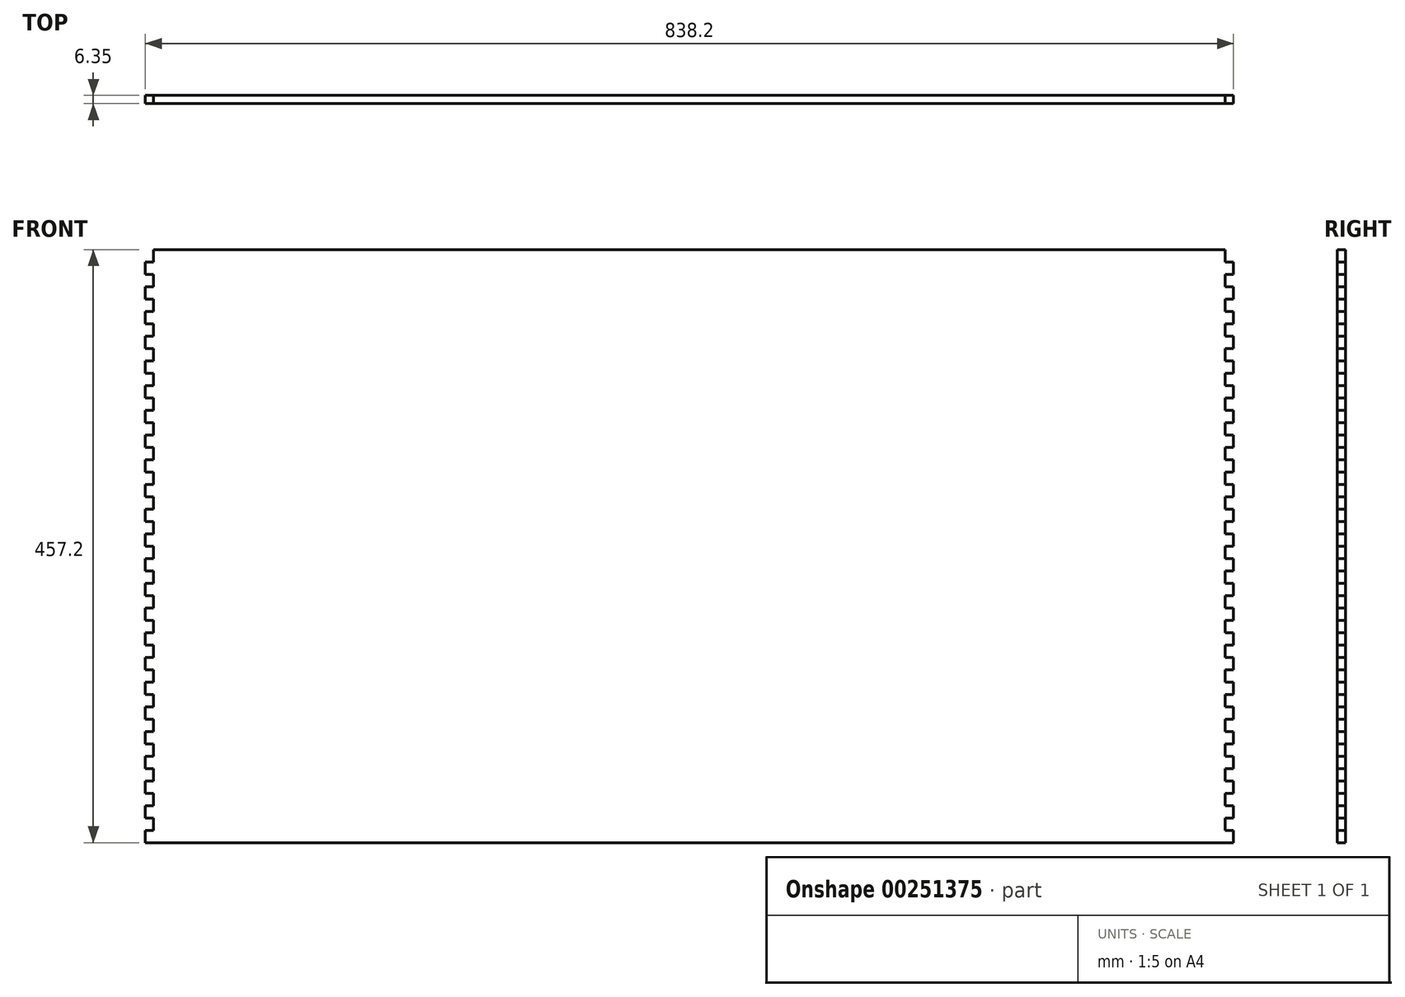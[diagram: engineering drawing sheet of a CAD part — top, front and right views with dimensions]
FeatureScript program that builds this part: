
annotation { "Feature Type Name" : "Feature", "Feature Type Description" : "" }
export const myFeature = defineFeature(function(context is Context, id is Id, definition is map)
    precondition{}
    {
        {
            var Q0;
            Q0=qCreatedBy(makeId("Front.planeOp"),FACE);
            var sketch = newSketch(context, id + "F0", { "sketchPlane" : qUnion([Q0])});
            skLineSegment(sketch, "E0.bottom", {"start": v(412.75, 228.6) * mm, "end": v(-412.75, 228.6) * mm});
            skLineSegment(sketch, "E0.top", {"start": v(419.1, -228.6) * mm, "end": v(-419.1, -228.6) * mm});
            skPoint(sketch, "E0.middle", {"position": v(0, 0) * mm});
            skLineSegment(sketch, "E1", {"start": v(412.75, 228.6) * mm, "end": v(412.75, 219.08) * mm});
            skLineSegment(sketch, "E2", {"start": v(412.75, 219.08) * mm, "end": v(419.1, 219.08) * mm});
            skLineSegment(sketch, "E3.0.1.0", {"start": v(412.75, 209.55) * mm, "end": v(412.75, 200.03) * mm});
            skLineSegment(sketch, "E3.0.1.1", {"start": v(412.75, 200.03) * mm, "end": v(419.1, 200.03) * mm});
            skLineSegment(sketch, "E3.0.1.3", {"start": v(419.1, 209.55) * mm, "end": v(412.75, 209.55) * mm});
            skLineSegment(sketch, "E3.0.2.0", {"start": v(412.75, 190.5) * mm, "end": v(412.75, 180.98) * mm});
            skLineSegment(sketch, "E3.0.2.1", {"start": v(412.75, 180.98) * mm, "end": v(419.1, 180.98) * mm});
            skLineSegment(sketch, "E3.0.2.3", {"start": v(419.1, 190.5) * mm, "end": v(412.75, 190.5) * mm});
            skLineSegment(sketch, "E3.0.3.0", {"start": v(412.75, 171.45) * mm, "end": v(412.75, 161.93) * mm});
            skLineSegment(sketch, "E3.0.3.1", {"start": v(412.75, 161.93) * mm, "end": v(419.1, 161.93) * mm});
            skLineSegment(sketch, "E3.0.3.3", {"start": v(419.1, 171.45) * mm, "end": v(412.75, 171.45) * mm});
            skLineSegment(sketch, "E3.0.4.0", {"start": v(412.75, 152.4) * mm, "end": v(412.75, 142.88) * mm});
            skLineSegment(sketch, "E3.0.4.1", {"start": v(412.75, 142.88) * mm, "end": v(419.1, 142.88) * mm});
            skLineSegment(sketch, "E3.0.4.3", {"start": v(419.1, 152.4) * mm, "end": v(412.75, 152.4) * mm});
            skLineSegment(sketch, "E3.0.5.0", {"start": v(412.75, 133.35) * mm, "end": v(412.75, 123.83) * mm});
            skLineSegment(sketch, "E3.0.5.1", {"start": v(412.75, 123.83) * mm, "end": v(419.1, 123.83) * mm});
            skLineSegment(sketch, "E3.0.5.3", {"start": v(419.1, 133.35) * mm, "end": v(412.75, 133.35) * mm});
            skLineSegment(sketch, "E3.0.6.0", {"start": v(412.75, 114.3) * mm, "end": v(412.75, 104.78) * mm});
            skLineSegment(sketch, "E3.0.6.1", {"start": v(412.75, 104.78) * mm, "end": v(419.1, 104.78) * mm});
            skLineSegment(sketch, "E3.0.6.3", {"start": v(419.1, 114.3) * mm, "end": v(412.75, 114.3) * mm});
            skLineSegment(sketch, "E3.0.7.0", {"start": v(412.75, 95.25) * mm, "end": v(412.75, 85.73) * mm});
            skLineSegment(sketch, "E3.0.7.1", {"start": v(412.75, 85.73) * mm, "end": v(419.1, 85.73) * mm});
            skLineSegment(sketch, "E3.0.7.3", {"start": v(419.1, 95.25) * mm, "end": v(412.75, 95.25) * mm});
            skLineSegment(sketch, "E3.0.8.0", {"start": v(412.75, 76.2) * mm, "end": v(412.75, 66.68) * mm});
            skLineSegment(sketch, "E3.0.8.1", {"start": v(412.75, 66.68) * mm, "end": v(419.1, 66.68) * mm});
            skLineSegment(sketch, "E3.0.8.3", {"start": v(419.1, 76.2) * mm, "end": v(412.75, 76.2) * mm});
            skLineSegment(sketch, "E3.0.9.0", {"start": v(412.75, 57.15) * mm, "end": v(412.75, 47.63) * mm});
            skLineSegment(sketch, "E3.0.9.1", {"start": v(412.75, 47.63) * mm, "end": v(419.1, 47.63) * mm});
            skLineSegment(sketch, "E3.0.9.3", {"start": v(419.1, 57.15) * mm, "end": v(412.75, 57.15) * mm});
            skLineSegment(sketch, "E3.0.10.0", {"start": v(412.75, 38.1) * mm, "end": v(412.75, 28.58) * mm});
            skLineSegment(sketch, "E3.0.10.1", {"start": v(412.75, 28.58) * mm, "end": v(419.1, 28.58) * mm});
            skLineSegment(sketch, "E3.0.10.3", {"start": v(419.1, 38.1) * mm, "end": v(412.75, 38.1) * mm});
            skLineSegment(sketch, "E3.0.11.0", {"start": v(412.75, 19.05) * mm, "end": v(412.75, 9.53) * mm});
            skLineSegment(sketch, "E3.0.11.1", {"start": v(412.75, 9.53) * mm, "end": v(419.1, 9.53) * mm});
            skLineSegment(sketch, "E3.0.11.3", {"start": v(419.1, 19.05) * mm, "end": v(412.75, 19.05) * mm});
            skLineSegment(sketch, "E3.0.12.0", {"start": v(412.75, 0) * mm, "end": v(412.75, -9.52) * mm});
            skLineSegment(sketch, "E3.0.12.1", {"start": v(412.75, -9.52) * mm, "end": v(419.1, -9.52) * mm});
            skLineSegment(sketch, "E3.0.12.3", {"start": v(419.1, 0) * mm, "end": v(412.75, 0) * mm});
            skLineSegment(sketch, "E3.0.13.0", {"start": v(412.75, -19.05) * mm, "end": v(412.75, -28.57) * mm});
            skLineSegment(sketch, "E3.0.13.1", {"start": v(412.75, -28.57) * mm, "end": v(419.1, -28.57) * mm});
            skLineSegment(sketch, "E3.0.13.3", {"start": v(419.1, -19.05) * mm, "end": v(412.75, -19.05) * mm});
            skLineSegment(sketch, "E3.0.14.0", {"start": v(412.75, -38.1) * mm, "end": v(412.75, -47.62) * mm});
            skLineSegment(sketch, "E3.0.14.1", {"start": v(412.75, -47.62) * mm, "end": v(419.1, -47.62) * mm});
            skLineSegment(sketch, "E3.0.14.3", {"start": v(419.1, -38.1) * mm, "end": v(412.75, -38.1) * mm});
            skLineSegment(sketch, "E3.0.15.0", {"start": v(412.75, -57.15) * mm, "end": v(412.75, -66.67) * mm});
            skLineSegment(sketch, "E3.0.15.1", {"start": v(412.75, -66.67) * mm, "end": v(419.1, -66.67) * mm});
            skLineSegment(sketch, "E3.0.15.3", {"start": v(419.1, -57.15) * mm, "end": v(412.75, -57.15) * mm});
            skLineSegment(sketch, "E3.0.16.0", {"start": v(412.75, -76.2) * mm, "end": v(412.75, -85.72) * mm});
            skLineSegment(sketch, "E3.0.16.1", {"start": v(412.75, -85.72) * mm, "end": v(419.1, -85.72) * mm});
            skLineSegment(sketch, "E3.0.16.3", {"start": v(419.1, -76.2) * mm, "end": v(412.75, -76.2) * mm});
            skLineSegment(sketch, "E3.0.17.0", {"start": v(412.75, -95.25) * mm, "end": v(412.75, -104.77) * mm});
            skLineSegment(sketch, "E3.0.17.1", {"start": v(412.75, -104.77) * mm, "end": v(419.1, -104.77) * mm});
            skLineSegment(sketch, "E3.0.17.3", {"start": v(419.1, -95.25) * mm, "end": v(412.75, -95.25) * mm});
            skLineSegment(sketch, "E3.0.18.0", {"start": v(412.75, -114.3) * mm, "end": v(412.75, -123.82) * mm});
            skLineSegment(sketch, "E3.0.18.1", {"start": v(412.75, -123.82) * mm, "end": v(419.1, -123.82) * mm});
            skLineSegment(sketch, "E3.0.18.3", {"start": v(419.1, -114.3) * mm, "end": v(412.75, -114.3) * mm});
            skLineSegment(sketch, "E3.0.19.0", {"start": v(412.75, -133.35) * mm, "end": v(412.75, -142.87) * mm});
            skLineSegment(sketch, "E3.0.19.1", {"start": v(412.75, -142.87) * mm, "end": v(419.1, -142.87) * mm});
            skLineSegment(sketch, "E3.0.19.3", {"start": v(419.1, -133.35) * mm, "end": v(412.75, -133.35) * mm});
            skLineSegment(sketch, "E3.0.20.0", {"start": v(412.75, -152.4) * mm, "end": v(412.75, -161.92) * mm});
            skLineSegment(sketch, "E3.0.20.1", {"start": v(412.75, -161.92) * mm, "end": v(419.1, -161.92) * mm});
            skLineSegment(sketch, "E3.0.20.3", {"start": v(419.1, -152.4) * mm, "end": v(412.75, -152.4) * mm});
            skLineSegment(sketch, "E3.0.21.0", {"start": v(412.75, -171.45) * mm, "end": v(412.75, -180.97) * mm});
            skLineSegment(sketch, "E3.0.21.1", {"start": v(412.75, -180.97) * mm, "end": v(419.1, -180.97) * mm});
            skLineSegment(sketch, "E3.0.21.3", {"start": v(419.1, -171.45) * mm, "end": v(412.75, -171.45) * mm});
            skLineSegment(sketch, "E3.0.22.0", {"start": v(412.75, -190.5) * mm, "end": v(412.75, -200.02) * mm});
            skLineSegment(sketch, "E3.0.22.1", {"start": v(412.75, -200.02) * mm, "end": v(419.1, -200.02) * mm});
            skLineSegment(sketch, "E3.0.22.3", {"start": v(419.1, -190.5) * mm, "end": v(412.75, -190.5) * mm});
            skLineSegment(sketch, "E3.0.23.0", {"start": v(412.75, -209.55) * mm, "end": v(412.75, -219.07) * mm});
            skLineSegment(sketch, "E3.0.23.1", {"start": v(412.75, -219.07) * mm, "end": v(419.1, -219.07) * mm});
            skLineSegment(sketch, "E3.0.23.3", {"start": v(419.1, -209.55) * mm, "end": v(412.75, -209.55) * mm});
            skLineSegment(sketch, "E3.direction1", {"start": v(412.75, 219.08) * mm, "end": v(422.15, 219.08) * mm, "construction": true});
            skLineSegment(sketch, "E3.direction2", {"start": v(412.75, 209.55) * mm, "end": v(412.75, 200.03) * mm, "construction": true});
            skLineSegment(sketch, "E4.trimOffspring", {"start": v(419.1, 200.03) * mm, "end": v(419.1, 190.5) * mm});
            skLineSegment(sketch, "E5", {"start": v(419.1, 209.55) * mm, "end": v(419.1, 219.08) * mm});
            skLineSegment(sketch, "E6", {"start": v(0, -228.6) * mm, "end": v(0, 228.6) * mm});
            skLineSegment(sketch, "E7.MirrorCS", {"start": v(-412.75, 219.08) * mm, "end": v(-419.1, 219.08) * mm});
            skLineSegment(sketch, "E8.MirrorCS", {"start": v(-412.75, 219.08) * mm, "end": v(-422.15, 219.08) * mm, "construction": true});
            skLineSegment(sketch, "E9.MirrorCS", {"start": v(-412.75, 209.55) * mm, "end": v(-412.75, 200.03) * mm});
            skLineSegment(sketch, "E10.MirrorCS", {"start": v(-419.1, 209.55) * mm, "end": v(-412.75, 209.55) * mm});
            skLineSegment(sketch, "E11.MirrorCS", {"start": v(-419.1, 171.45) * mm, "end": v(-412.75, 171.45) * mm});
            skLineSegment(sketch, "E12.MirrorCS", {"start": v(-412.75, -76.2) * mm, "end": v(-412.75, -85.72) * mm});
            skLineSegment(sketch, "E13.MirrorCS", {"start": v(-412.75, 76.2) * mm, "end": v(-412.75, 66.68) * mm});
            skLineSegment(sketch, "E14.MirrorCS", {"start": v(-412.75, 209.55) * mm, "end": v(-412.75, 200.03) * mm, "construction": true});
            skLineSegment(sketch, "E15.MirrorCS", {"start": v(-412.75, 180.98) * mm, "end": v(-419.1, 180.98) * mm});
            skLineSegment(sketch, "E16.MirrorCS", {"start": v(-419.1, 190.5) * mm, "end": v(-412.75, 190.5) * mm});
            skLineSegment(sketch, "E17.MirrorCS", {"start": v(-412.75, 200.03) * mm, "end": v(-419.1, 200.03) * mm});
            skLineSegment(sketch, "E18.MirrorCS", {"start": v(-412.75, 190.5) * mm, "end": v(-412.75, 180.98) * mm});
            skLineSegment(sketch, "E19.MirrorCS", {"start": v(-419.1, 76.2) * mm, "end": v(-412.75, 76.2) * mm});
            skLineSegment(sketch, "E20.MirrorCS", {"start": v(-419.1, -76.2) * mm, "end": v(-412.75, -76.2) * mm});
            skLineSegment(sketch, "E21.MirrorCS", {"start": v(-412.75, 171.45) * mm, "end": v(-412.75, 161.93) * mm});
            skLineSegment(sketch, "E22.MirrorCS", {"start": v(-412.75, 95.25) * mm, "end": v(-412.75, 85.73) * mm});
            skLineSegment(sketch, "E23.MirrorCS", {"start": v(-412.75, -57.15) * mm, "end": v(-412.75, -66.67) * mm});
            skLineSegment(sketch, "E24.MirrorCS", {"start": v(-412.75, -66.67) * mm, "end": v(-419.1, -66.67) * mm});
            skLineSegment(sketch, "E25.MirrorCS", {"start": v(-412.75, 85.73) * mm, "end": v(-419.1, 85.73) * mm});
            skLineSegment(sketch, "E26.MirrorCS", {"start": v(-419.1, 95.25) * mm, "end": v(-412.75, 95.25) * mm});
            skLineSegment(sketch, "E27.MirrorCS", {"start": v(-419.1, -57.15) * mm, "end": v(-412.75, -57.15) * mm});
            skLineSegment(sketch, "E28.MirrorCS", {"start": v(-419.1, -19.05) * mm, "end": v(-412.75, -19.05) * mm});
            skLineSegment(sketch, "E29.MirrorCS", {"start": v(-419.1, 57.15) * mm, "end": v(-412.75, 57.15) * mm});
            skLineSegment(sketch, "E30.MirrorCS", {"start": v(-419.1, 133.35) * mm, "end": v(-412.75, 133.35) * mm});
            skLineSegment(sketch, "E31.MirrorCS", {"start": v(-419.1, -171.45) * mm, "end": v(-412.75, -171.45) * mm});
            skLineSegment(sketch, "E32.MirrorCS", {"start": v(-412.75, 152.4) * mm, "end": v(-412.75, 142.88) * mm});
            skLineSegment(sketch, "E33.MirrorCS", {"start": v(-419.1, -95.25) * mm, "end": v(-412.75, -95.25) * mm});
            skLineSegment(sketch, "E34.MirrorCS", {"start": v(-412.75, -152.4) * mm, "end": v(-412.75, -161.92) * mm});
            skLineSegment(sketch, "E35.MirrorCS", {"start": v(-412.75, -123.82) * mm, "end": v(-419.1, -123.82) * mm});
            skLineSegment(sketch, "E36.MirrorCS", {"start": v(-412.75, -47.62) * mm, "end": v(-419.1, -47.62) * mm});
            skLineSegment(sketch, "E37.MirrorCS", {"start": v(-419.1, -209.55) * mm, "end": v(-412.75, -209.55) * mm});
            skLineSegment(sketch, "E38.MirrorCS", {"start": v(-412.75, 28.58) * mm, "end": v(-419.1, 28.58) * mm});
            skLineSegment(sketch, "E39.MirrorCS", {"start": v(-412.75, 0) * mm, "end": v(-412.75, -9.52) * mm});
            skLineSegment(sketch, "E40.MirrorCS", {"start": v(-412.75, 104.78) * mm, "end": v(-419.1, 104.78) * mm});
            skLineSegment(sketch, "E41.MirrorCS", {"start": v(-412.75, -200.02) * mm, "end": v(-419.1, -200.02) * mm});
            skLineSegment(sketch, "E42.MirrorCS", {"start": v(-412.75, -38.1) * mm, "end": v(-412.75, -47.62) * mm});
            skLineSegment(sketch, "E43.MirrorCS", {"start": v(-412.75, 38.1) * mm, "end": v(-412.75, 28.58) * mm});
            skLineSegment(sketch, "E44.MirrorCS", {"start": v(-412.75, 114.3) * mm, "end": v(-412.75, 104.78) * mm});
            skLineSegment(sketch, "E45.MirrorCS", {"start": v(-412.75, -114.3) * mm, "end": v(-412.75, -123.82) * mm});
            skLineSegment(sketch, "E46.MirrorCS", {"start": v(-412.75, -190.5) * mm, "end": v(-412.75, -200.02) * mm});
            skLineSegment(sketch, "E47.MirrorCS", {"start": v(-412.75, 142.88) * mm, "end": v(-419.1, 142.88) * mm});
            skLineSegment(sketch, "E48.MirrorCS", {"start": v(-412.75, -161.92) * mm, "end": v(-419.1, -161.92) * mm});
            skLineSegment(sketch, "E49.MirrorCS", {"start": v(-412.75, -85.72) * mm, "end": v(-419.1, -85.72) * mm});
            skLineSegment(sketch, "E50.MirrorCS", {"start": v(-412.75, 66.68) * mm, "end": v(-419.1, 66.68) * mm});
            skLineSegment(sketch, "E51.MirrorCS", {"start": v(-412.75, -9.52) * mm, "end": v(-419.1, -9.52) * mm});
            skLineSegment(sketch, "E52.MirrorCS", {"start": v(-419.1, -114.3) * mm, "end": v(-412.75, -114.3) * mm});
            skLineSegment(sketch, "E53.MirrorCS", {"start": v(-419.1, -38.1) * mm, "end": v(-412.75, -38.1) * mm});
            skLineSegment(sketch, "E54.MirrorCS", {"start": v(-419.1, 38.1) * mm, "end": v(-412.75, 38.1) * mm});
            skLineSegment(sketch, "E55.MirrorCS", {"start": v(-419.1, 114.3) * mm, "end": v(-412.75, 114.3) * mm});
            skLineSegment(sketch, "E56.MirrorCS", {"start": v(-419.1, -190.5) * mm, "end": v(-412.75, -190.5) * mm});
            skLineSegment(sketch, "E57.MirrorCS", {"start": v(-412.75, -209.55) * mm, "end": v(-412.75, -219.07) * mm});
            skLineSegment(sketch, "E58.MirrorCS", {"start": v(-419.1, 0) * mm, "end": v(-412.75, 0) * mm});
            skLineSegment(sketch, "E59.MirrorCS", {"start": v(-419.1, 152.4) * mm, "end": v(-412.75, 152.4) * mm});
            skLineSegment(sketch, "E60.MirrorCS", {"start": v(-419.1, -152.4) * mm, "end": v(-412.75, -152.4) * mm});
            skLineSegment(sketch, "E61.MirrorCS", {"start": v(-412.75, -133.35) * mm, "end": v(-412.75, -142.87) * mm});
            skLineSegment(sketch, "E62.MirrorCS", {"start": v(-412.75, 19.05) * mm, "end": v(-412.75, 9.53) * mm});
            skLineSegment(sketch, "E63.MirrorCS", {"start": v(-412.75, 133.35) * mm, "end": v(-412.75, 123.83) * mm});
            skLineSegment(sketch, "E64.MirrorCS", {"start": v(-412.75, -19.05) * mm, "end": v(-412.75, -28.57) * mm});
            skLineSegment(sketch, "E65.MirrorCS", {"start": v(-412.75, 57.15) * mm, "end": v(-412.75, 47.63) * mm});
            skLineSegment(sketch, "E66.MirrorCS", {"start": v(-412.75, -171.45) * mm, "end": v(-412.75, -180.97) * mm});
            skLineSegment(sketch, "E67.MirrorCS", {"start": v(-412.75, -95.25) * mm, "end": v(-412.75, -104.77) * mm});
            skLineSegment(sketch, "E68.MirrorCS", {"start": v(-412.75, 161.93) * mm, "end": v(-419.1, 161.93) * mm});
            skLineSegment(sketch, "E69.MirrorCS", {"start": v(-412.75, -142.87) * mm, "end": v(-419.1, -142.87) * mm});
            skLineSegment(sketch, "E70.MirrorCS", {"start": v(-412.75, 9.53) * mm, "end": v(-419.1, 9.53) * mm});
            skLineSegment(sketch, "E71.MirrorCS", {"start": v(-412.75, -219.07) * mm, "end": v(-419.1, -219.07) * mm});
            skLineSegment(sketch, "E72.MirrorCS", {"start": v(-412.75, -28.57) * mm, "end": v(-419.1, -28.57) * mm});
            skLineSegment(sketch, "E73.MirrorCS", {"start": v(-412.75, 47.63) * mm, "end": v(-419.1, 47.63) * mm});
            skLineSegment(sketch, "E74.MirrorCS", {"start": v(-412.75, 123.83) * mm, "end": v(-419.1, 123.83) * mm});
            skLineSegment(sketch, "E75.MirrorCS", {"start": v(-419.1, -133.35) * mm, "end": v(-412.75, -133.35) * mm});
            skLineSegment(sketch, "E76.MirrorCS", {"start": v(-412.75, -104.77) * mm, "end": v(-419.1, -104.77) * mm});
            skLineSegment(sketch, "E77.MirrorCS", {"start": v(-412.75, -180.97) * mm, "end": v(-419.1, -180.97) * mm});
            skLineSegment(sketch, "E78.MirrorCS", {"start": v(-419.1, 19.05) * mm, "end": v(-412.75, 19.05) * mm});
            skLineSegment(sketch, "E79.trimOffspring", {"start": v(-419.1, 180.98) * mm, "end": v(-419.1, 171.45) * mm});
            skLineSegment(sketch, "E80", {"start": v(-419.1, 209.55) * mm, "end": v(-419.1, 219.08) * mm});
            skLineSegment(sketch, "E81", {"start": v(-419.1, 200.03) * mm, "end": v(-419.1, 190.5) * mm});
            skLineSegment(sketch, "E82", {"start": v(-412.75, 219.08) * mm, "end": v(-412.75, 228.6) * mm});
            skPoint(sketch, "E83.MirrorCS.start.orphan", {"position": v(-419.1, 228.6) * mm});
            skPoint(sketch, "E84.trimOffspring.start.orphan", {"position": v(-419.1, 209.55) * mm});
            skPoint(sketch, "E85.MirrorCS.end.orphan", {"position": v(-419.1, 171.45) * mm});
            skLineSegment(sketch, "E86.trimOffspring", {"start": v(-419.1, 161.93) * mm, "end": v(-419.1, 152.4) * mm});
            skLineSegment(sketch, "E87.trimOffspring", {"start": v(-419.1, 142.88) * mm, "end": v(-419.1, 133.35) * mm});
            skPoint(sketch, "E88.MirrorCS.end.orphan", {"position": v(-419.1, 152.4) * mm});
            skPoint(sketch, "E89.MirrorCS.end.orphan", {"position": v(-419.1, 133.35) * mm});
            skLineSegment(sketch, "E90.trimOffspring", {"start": v(-419.1, 123.83) * mm, "end": v(-419.1, 114.3) * mm});
            skPoint(sketch, "E91.MirrorCS.end.orphan", {"position": v(-419.1, 114.3) * mm});
            skLineSegment(sketch, "E92.trimOffspring", {"start": v(-419.1, 104.78) * mm, "end": v(-419.1, 95.25) * mm});
            skPoint(sketch, "E93.MirrorCS.end.orphan", {"position": v(-419.1, 95.25) * mm});
            skLineSegment(sketch, "E94.trimOffspring", {"start": v(-419.1, 85.73) * mm, "end": v(-419.1, 76.2) * mm});
            skLineSegment(sketch, "E95.trimOffspring", {"start": v(-419.1, 66.68) * mm, "end": v(-419.1, 57.15) * mm});
            skPoint(sketch, "E96.MirrorCS.end.orphan", {"position": v(-419.1, 57.15) * mm});
            skLineSegment(sketch, "E97.trimOffspring", {"start": v(-419.1, 47.63) * mm, "end": v(-419.1, 38.1) * mm});
            skPoint(sketch, "E98.MirrorCS.end.orphan", {"position": v(-419.1, 38.1) * mm});
            skLineSegment(sketch, "E99.trimOffspring", {"start": v(-419.1, 28.58) * mm, "end": v(-419.1, 19.05) * mm});
            skPoint(sketch, "E100.MirrorCS.end.orphan", {"position": v(-419.1, 19.05) * mm});
            skLineSegment(sketch, "E101", {"start": v(-419.1, 9.53) * mm, "end": v(-419.1, 0) * mm});
            skLineSegment(sketch, "E102", {"start": v(-419.1, -9.52) * mm, "end": v(-419.1, -19.05) * mm});
            skLineSegment(sketch, "E103", {"start": v(-419.1, -28.57) * mm, "end": v(-419.1, -38.1) * mm});
            skLineSegment(sketch, "E104", {"start": v(-419.1, -47.62) * mm, "end": v(-419.1, -57.15) * mm});
            skLineSegment(sketch, "E105", {"start": v(-419.1, -66.67) * mm, "end": v(-419.1, -76.2) * mm});
            skLineSegment(sketch, "E106", {"start": v(-419.1, -85.72) * mm, "end": v(-419.1, -95.25) * mm});
            skLineSegment(sketch, "E107", {"start": v(-419.1, -104.77) * mm, "end": v(-419.1, -114.3) * mm});
            skPoint(sketch, "E108.MirrorCS.end.orphan", {"position": v(-412.75, -133.35) * mm});
            skPoint(sketch, "E109.MirrorCS.end.orphan", {"position": v(-412.75, -152.4) * mm});
            skPoint(sketch, "E110.MirrorCS.end.orphan", {"position": v(-419.1, -171.45) * mm});
            skPoint(sketch, "E111.MirrorCS.end.orphan", {"position": v(-419.1, -190.5) * mm});
            skPoint(sketch, "E112.MirrorCS.end.orphan", {"position": v(-419.1, -209.55) * mm});
            skLineSegment(sketch, "E113", {"start": v(-419.1, -123.82) * mm, "end": v(-419.1, -133.35) * mm});
            skLineSegment(sketch, "E114", {"start": v(-419.1, -142.87) * mm, "end": v(-419.1, -152.4) * mm});
            skLineSegment(sketch, "E115", {"start": v(-419.1, -161.92) * mm, "end": v(-419.1, -171.45) * mm});
            skLineSegment(sketch, "E116", {"start": v(-419.1, -180.97) * mm, "end": v(-419.1, -190.5) * mm});
            skLineSegment(sketch, "E117", {"start": v(-419.1, -200.02) * mm, "end": v(-419.1, -209.55) * mm});
            skLineSegment(sketch, "E118", {"start": v(-419.1, -219.07) * mm, "end": v(-419.1, -228.6) * mm});
            skPoint(sketch, "E3.0.23.2.end.orphan", {"position": v(419.1, -209.55) * mm});
            skLineSegment(sketch, "E119.trimOffspring", {"start": v(419.1, -219.07) * mm, "end": v(419.1, -228.6) * mm});
            skPoint(sketch, "E3.0.22.2.end.orphan", {"position": v(419.1, -190.5) * mm});
            skLineSegment(sketch, "E120.trimOffspring", {"start": v(419.1, -200.02) * mm, "end": v(419.1, -209.55) * mm});
            skPoint(sketch, "E3.0.21.2.end.orphan", {"position": v(419.1, -171.45) * mm});
            skLineSegment(sketch, "E121.trimOffspring", {"start": v(419.1, -180.97) * mm, "end": v(419.1, -190.5) * mm});
            skLineSegment(sketch, "E122.trimOffspring", {"start": v(419.1, -161.92) * mm, "end": v(419.1, -171.45) * mm});
            skPoint(sketch, "E3.0.20.2.end.orphan", {"position": v(412.75, -152.4) * mm});
            skLineSegment(sketch, "E123.trimOffspring", {"start": v(419.1, -142.87) * mm, "end": v(419.1, -152.4) * mm});
            skPoint(sketch, "E3.0.19.2.end.orphan", {"position": v(412.75, -133.35) * mm});
            skLineSegment(sketch, "E124.trimOffspring", {"start": v(419.1, -123.82) * mm, "end": v(419.1, -133.35) * mm});
            skPoint(sketch, "E3.0.18.2.end.orphan", {"position": v(419.1, -114.3) * mm});
            skLineSegment(sketch, "E125.trimOffspring", {"start": v(419.1, -104.77) * mm, "end": v(419.1, -114.3) * mm});
            skLineSegment(sketch, "E126.trimOffspring", {"start": v(419.1, -85.72) * mm, "end": v(419.1, -95.25) * mm});
            skLineSegment(sketch, "E127.trimOffspring", {"start": v(419.1, -66.67) * mm, "end": v(419.1, -76.2) * mm});
            skLineSegment(sketch, "E128.trimOffspring", {"start": v(419.1, -47.62) * mm, "end": v(419.1, -57.15) * mm});
            skLineSegment(sketch, "E129.trimOffspring", {"start": v(419.1, -28.57) * mm, "end": v(419.1, -38.1) * mm});
            skLineSegment(sketch, "E130.trimOffspring", {"start": v(419.1, -9.52) * mm, "end": v(419.1, -19.05) * mm});
            skPoint(sketch, "E3.0.11.2.end.orphan", {"position": v(419.1, 19.05) * mm});
            skPoint(sketch, "E3.0.10.2.end.orphan", {"position": v(419.1, 38.1) * mm});
            skLineSegment(sketch, "E131.trimOffspring", {"start": v(419.1, 47.63) * mm, "end": v(419.1, 38.1) * mm});
            skLineSegment(sketch, "E132.trimOffspring", {"start": v(419.1, 66.68) * mm, "end": v(419.1, 57.15) * mm});
            skPoint(sketch, "E3.0.8.2.end.orphan", {"position": v(419.1, 76.2) * mm});
            skPoint(sketch, "E3.0.9.2.end.orphan", {"position": v(419.1, 57.15) * mm});
            skLineSegment(sketch, "E133.trimOffspring", {"start": v(419.1, 28.58) * mm, "end": v(419.1, 19.05) * mm});
            skLineSegment(sketch, "E134.trimOffspring", {"start": v(419.1, 9.53) * mm, "end": v(419.1, 0) * mm});
            skPoint(sketch, "E3.0.7.2.end.orphan", {"position": v(419.1, 95.25) * mm});
            skLineSegment(sketch, "E135.trimOffspring", {"start": v(419.1, 85.73) * mm, "end": v(419.1, 76.2) * mm});
            skPoint(sketch, "E3.0.6.2.end.orphan", {"position": v(419.1, 114.3) * mm});
            skLineSegment(sketch, "E136.trimOffspring", {"start": v(419.1, 104.78) * mm, "end": v(419.1, 95.25) * mm});
            skPoint(sketch, "E3.0.5.2.end.orphan", {"position": v(419.1, 133.35) * mm});
            skLineSegment(sketch, "E137.trimOffspring", {"start": v(419.1, 142.88) * mm, "end": v(419.1, 133.35) * mm});
            skLineSegment(sketch, "E138.trimOffspring", {"start": v(419.1, 161.93) * mm, "end": v(419.1, 152.4) * mm});
            skLineSegment(sketch, "E139.trimOffspring", {"start": v(419.1, 123.83) * mm, "end": v(419.1, 114.3) * mm});
            skLineSegment(sketch, "E140.trimOffspring", {"start": v(419.1, 180.98) * mm, "end": v(419.1, 171.45) * mm});
            skPoint(sketch, "E3.0.2.2.end.orphan", {"position": v(419.1, 190.5) * mm});
            skPoint(sketch, "E0.left.start.orphan", {"position": v(419.1, 228.6) * mm});
            skSolve(sketch);
        }
        {
            var Q0;
            Q0 = qSketchRegion(id + "F0", true);
            extrude(context, id + "F1", {"entities" : qUnion([Q0]), "depth" : 6.35 * mm});
        }
    });
